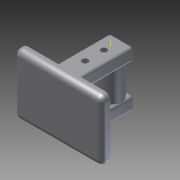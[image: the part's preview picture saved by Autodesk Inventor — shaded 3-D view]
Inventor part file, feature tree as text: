
AUTODESK INVENTOR PART (.ipt)
format: ipt  version: 2012 (Build 160160000, 160)  size: 377,344 bytes
history: native  units: in
note: dims shown in document units (in); Inventor stores cm internally (conversion verified against a paired STEP export)
features: fillet x10, extrude x6, sketch x6, other x4, projected_geometry x3
ambient origin geometry x8: Origin, YZ Plane, XZ Plane, XY Plane, X Axis, Y Axis, Z Axis, Center Point
bodies: Solid1 (feature_tree)
feature tree (29):
  other  "TopAndIntermediaryAxle"
  other  "GearBoxTop.ipt:1"
  other  "LargeSmallGearAxis.ipt:1"
  extrude  "Extrusion1"  Depth=0.3937in TaperAngle=0.0deg
  extrude  "Extrusion2"  Depth=0.0787in
  fillet  "Fillet1"  Radius=0.0787in
  fillet  "Fillet2"  Radius=0.0787in
  fillet  "Fillet3"  Radius=0.0787in
  fillet  "Fillet4"  Radius=0.0787in
  fillet  "Fillet5"  Radius=0.0394in
  fillet  "Fillet6"  Radius=0.0394in
  fillet  "Fillet7"  Radius=0.0394in
  fillet  "Fillet8"  Radius=0.0394in
  fillet  "Fillet9"  Radius=0.0394in
  fillet  "Fillet10"  Radius=0.269in
  extrude  "Extrusion4"  Depth=0.1181in TaperAngle=0.0deg
  extrude  "Extrusion5"  Depth=0.2657in
  extrude  "Extrusion3"  Depth=0.1329in
  extrude  "Extrusion6"  Depth=0.0866in
  other  "Work Axis1"
  sketch  "Sketch2"  dims[d0=0.3937in d1=0.3937in d2=0.0in]
  projected_geometry  "Projected Loop1"
  sketch  "Sketch3"  dims[d3=0.3937in d4=0.0in d5=0.0787in d6=0.0787in d7=0.0787in d8=0.0787in d9=0.0787in d10=0.0394in d11=0.0394in d12=0.0394in d13=0.0394in d14=0.0394in d15=0.269in]
  projected_geometry  "Projected Loop2"
  sketch  "Sketch4"  dims[d18=0.7964in d19=0.1181in d20=0.0in]
  projected_geometry  "Projected Loop3"
  sketch  "Sketch5"  dims[d21=0.1181in d22=0.0in d23=0.2657in]
  sketch  "Sketch6"  dims[d24=0.1329in d25=0.1329in]
  sketch  "Sketch7"  dims[d26=0.0866in d27=0.0866in d28=0.1181in d29=0.0in d30=0.269in d31=0.1181in d32=0.0in]
